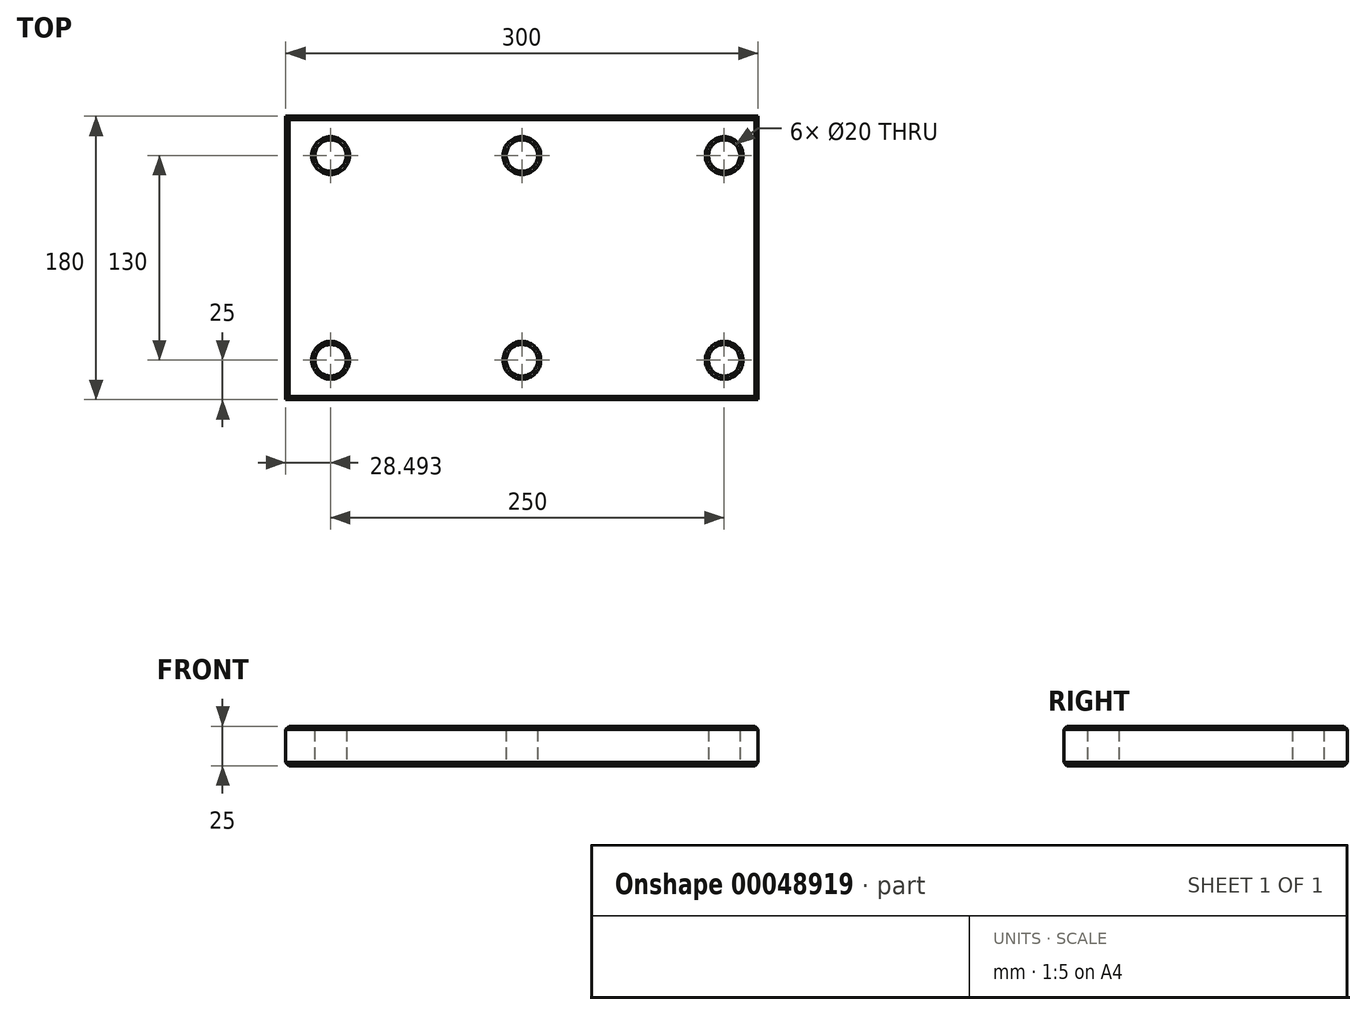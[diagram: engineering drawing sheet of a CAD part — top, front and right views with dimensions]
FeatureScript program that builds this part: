
annotation { "Feature Type Name" : "Feature", "Feature Type Description" : "" }
export const myFeature = defineFeature(function(context is Context, id is Id, definition is map)
    precondition{}
    {
        {
            var Q0;
            Q0=qCreatedBy(makeId("Top.planeOp"),FACE);
            var sketch = newSketch(context, id + "F0", { "sketchPlane" : qUnion([Q0])});
            skLineSegment(sketch, "E0.rect.bottom", {"start": v(150, 90) * mm, "end": v(-150, 90) * mm});
            skLineSegment(sketch, "E0.rect.top", {"start": v(150, -90) * mm, "end": v(-150, -90) * mm});
            skLineSegment(sketch, "E0.rect.left", {"start": v(150, 90) * mm, "end": v(150, -90) * mm});
            skLineSegment(sketch, "E0.rect.right", {"start": v(-150, 90) * mm, "end": v(-150, -90) * mm});
            skPoint(sketch, "E0.rect.middle", {"position": v(0, 0) * mm});
            skCircle(sketch, "E1", {"center": v(0, 65) * mm, "radius": 10 * mm});
            skCircle(sketch, "E2", {"center": v(-121.5, 65) * mm, "radius": 10 * mm});
            skCircle(sketch, "E3", {"center": v(128.5, 65) * mm, "radius": 10 * mm});
            skCircle(sketch, "E4.MirrorC", {"center": v(128.5, -65) * mm, "radius": 10 * mm});
            skCircle(sketch, "E5.MirrorC", {"center": v(0, -65) * mm, "radius": 10 * mm});
            skCircle(sketch, "E6.MirrorC", {"center": v(-121.5, -65) * mm, "radius": 10 * mm});
            skSolve(sketch);
        }
        {
            var Q0;
            Q0=makeQuery(id+"F0.imprint","IMPRINT",FACE,{"disambiguationData":[TD([[makeQuery(id+"F0.imprint","IMPRINT",EDGE,{"derivedFrom":sQuery(id+"F0.wireOp",EDGE,"E0.rect.bottom")}),1.0]])]});
            extrude(context, id + "F1", {"entities" : qUnion([Q0]), "depth" : 25 * mm});
        }
        {
            var Q0;
            Q0=makeQuery(id+"F1.opExtrude","CAP_FACE",FACE,{"disambiguationData":[OSD([sQuery(id+"F0.wireOp",EDGE,"E0.rect.bottom"),sQuery(id+"F0.wireOp",EDGE,"E0.rect.top"),sQuery(id+"F0.wireOp",EDGE,"E0.rect.left"),sQuery(id+"F0.wireOp",EDGE,"E0.rect.right"),sQuery(id+"F0.wireOp",EDGE,"E1"),sQuery(id+"F0.wireOp",EDGE,"E2"),sQuery(id+"F0.wireOp",EDGE,"E3"),sQuery(id+"F0.wireOp",EDGE,"E4.MirrorC"),sQuery(id+"F0.wireOp",EDGE,"E5.MirrorC"),sQuery(id+"F0.wireOp",EDGE,"E6.MirrorC")])],"isStart":false});
            var Q1;
            Q1=makeQuery(id+"F1.opExtrude","CAP_FACE",FACE,{"disambiguationData":[OSD([sQuery(id+"F0.wireOp",EDGE,"E0.rect.bottom"),sQuery(id+"F0.wireOp",EDGE,"E0.rect.top"),sQuery(id+"F0.wireOp",EDGE,"E0.rect.left"),sQuery(id+"F0.wireOp",EDGE,"E0.rect.right"),sQuery(id+"F0.wireOp",EDGE,"E1"),sQuery(id+"F0.wireOp",EDGE,"E2"),sQuery(id+"F0.wireOp",EDGE,"E3"),sQuery(id+"F0.wireOp",EDGE,"E4.MirrorC"),sQuery(id+"F0.wireOp",EDGE,"E5.MirrorC"),sQuery(id+"F0.wireOp",EDGE,"E6.MirrorC")])],"isStart":true});
            chamfer(context, id + "F2", {"entities" : qUnion([Q0, Q1]), "width" : 2 * mm, "tangentPropagation" : true});
        }
    });
